# Revit family: IS_Tesi_T3510_BIM_FR
name_source: partatom
category: Plumbing Fixtures
revit_build: Autodesk Revit 2017 (Build: 20160225_1515(x64)
units: mm (PartAtom-declared; Revit-internal decimal feet)

## family parameters
Cut with Voids When Loaded = No
Host = Face
OmniClass Number = 23.45.00.00
OmniClass Title = Sanitary, Laundry, and Cleaning Equipment
Part Type = Normal
Room Calculation Point = No
Round Connector Dimension = Use Diameter
Shared = No

## types (1)
- IS_Tesi_T3510_BIM_FR
    Accessoires = www.idealstandard.be
    Assembly Code = C1030200
    Bim-NomDuProjet = ISI_IdealStandard_Tesi_T3510
    CWFU = 0
    Caractéristiques = Lavabo-Plan 62,5 x 45 cm
    CodeBarre = 8014140430155
    ConseilsDInstallation = www.idealstandard.be
    Cost = 0 $
    Couleur = Blanc
    CoûtDeRemplacement = 0
    DateDeCréation = 2018_08_15
    Default Elevation = 0 mm  [stored 0 ft]
    Description = Lavabo-Plan 62,5 x 45 cm
    Dimensions = 0 x 0 x 0 mm
    Espace = Interne
    Finition = Blanc
    Forme = Complexe
    HWFU = 0
    Hauteur = 0 mm  [stored 0 ft]
    IfcExportAs = IfcSanitaryTerminalType
    IfcExportType = WASHHANDBASINS
    InformationsProduit = www.idealstandard.be
    Largeur = 0 mm  [stored 0 ft]
    LienUtile = www.idealstandard.be
    Longueur = 0 mm  [stored 0 ft]
    Manufacturer = www.idealstandard.be
    Marque = Ideal Standard
    Matériel = Vitreous China
    Model = T351001
    PoidsNet = 13.40 Kg
    Profondeur = 0 mm  [stored 0 ft]
    Raccordement = Plomberie
    Révision = 1
    URL = www.idealstandard.be
    Uniclass2015Code = Pr_40_20_96_96
    Uniclass2015Title = Wall-hung wash basins
    UnitéDeMesure = Millimètres
    UnitéDeTemps = An
    UnitéMonétaire = €
    UrlDuFabricant = www.idealstandard.be
    WFU = 0

note: [stored X ft] marks values corroborated as IEEE doubles in the binary element streams (Revit-internal decimal feet)

## geometry (parser evidence)
native form markers: Sweep x3
no freeform markers — native parametric forms only
